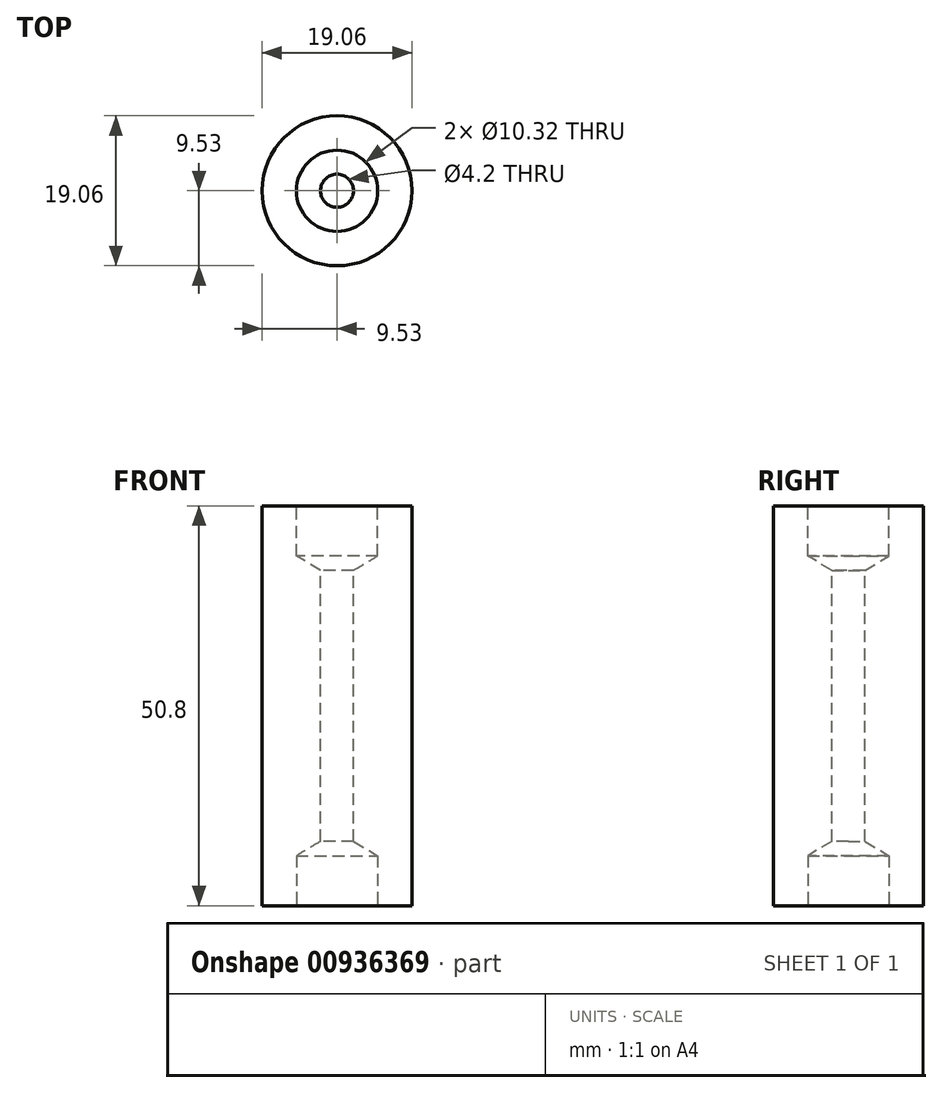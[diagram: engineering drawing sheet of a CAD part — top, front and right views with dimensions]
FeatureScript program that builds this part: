
annotation { "Feature Type Name" : "Feature", "Feature Type Description" : "" }
export const myFeature = defineFeature(function(context is Context, id is Id, definition is map)
    precondition{}
    {
        {
            var Q0;
            Q0=qCreatedBy(makeId("Top.planeOp"),FACE);
            cPlane(context, id + "F0", {"entities" : qUnion([Q0]), "cplaneType" : CPlaneType.OFFSET, "offset" : 50.8 * mm, "oppositeDirection" : true, "width" : 152.4 * mm, "height" : 152.4 * mm});
        }
        {
            var Q0;
            Q0=qCreatedBy(makeId("Top.planeOp"),FACE);
            var sketch = newSketch(context, id + "F1", { "sketchPlane" : qUnion([Q0])});
            skCircle(sketch, "E0", {"center": v(0, 0) * mm, "radius": 9.53 * mm});
            skSolve(sketch);
        }
        {
            var Q0;
            Q0=makeQuery(id+"F1.imprint","IMPRINT",FACE,{"disambiguationData":[TD([[makeQuery(id+"F1.imprint","IMPRINT",EDGE,{"derivedFrom":sQuery(id+"F1.wireOp",EDGE,"E0")}),1.0]])]});
            var Q1;
            Q1=qCreatedBy(id+"F0.planeOp",FACE);
            extrude(context, id + "F2", {"entities" : qUnion([Q0]), "endBound" : BoundingType.UP_TO_SURFACE, "oppositeDirection" : true, "depth" : 25.4 * mm, "endBoundEntityFace" : qUnion([Q1]), "offsetDistance" : 25.4 * mm});
        }
        {
            var Q0;
            Q0=qCreatedBy(makeId("Top.planeOp"),FACE);
            var sketch = newSketch(context, id + "F3", { "sketchPlane" : qUnion([Q0])});
            skPoint(sketch, "E1", {"position": v(0, 0) * mm});
            skSolve(sketch);
        }
        {
            var Q0;
            Q0=qCreatedBy(id+"F0.planeOp",FACE);
            var sketch = newSketch(context, id + "F4", { "sketchPlane" : qUnion([Q0])});
            skPoint(sketch, "E2", {"position": v(0, 0) * mm});
            skSolve(sketch);
        }
        {
            var Q0;
            Q0=sQuery(id+"F3.wireOp",VERTEX,"E1");
            var Q1;
            Q1=makeQuery(id+"F2.opExtrude","SWEPT_BODY",BODY,{"disambiguationData":[OSD([sQuery(id+"F1.wireOp",EDGE,"E0")])]});
            hole(context, id + "F5", {"style" : HoleStyle.SIMPLE, "endStyle" : HoleEndStyle.THROUGH, "standardTappedOrClearance" : lookupTablePath({ "standard" : "ISO", "engagement" : "75%", "pitch" : "0.8 mm", "size" : "M5", "type" : "Tapped" }), "standardBlindInLast" : lookupTablePath({ "standard" : "ISO", "fit" : "Normal", "engagement" : "75%", "pitch" : "0.8 mm", "size" : "M5", "type" : "Clearance & tapped" }), "holeDiameter" : 4.2 * mm, "majorDiameter" : 5 * mm, "showTappedDepth" : true, "tappedDepth" : 12.7 * mm, "tapClearance" : 3, "locations" : qUnion([Q0]), "scope" : qUnion([Q1])});
        }
        {
            var Q0;
            Q0=sQuery(id+"F4.wireOp",VERTEX,"E2");
            var Q1;
            Q1=makeQuery(id+"F2.opExtrude","SWEPT_BODY",BODY,{"disambiguationData":[OSD([sQuery(id+"F1.wireOp",EDGE,"E0")])]});
            hole(context, id + "F6", {"style" : HoleStyle.SIMPLE, "endStyle" : HoleEndStyle.BLIND, "oppositeDirection" : true, "holeDiameter" : 10.32 * mm, "majorDiameter" : 6.35 * mm, "holeDepth" : 6.35 * mm, "tappedDepth" : 12.7 * mm, "tapClearance" : 3, "startFromSketch" : true, "locations" : qUnion([Q0]), "scope" : qUnion([Q1])});
        }
        {
            var Q0;
            Q0=qCreatedBy(makeId("Top.planeOp"),FACE);
            var sketch = newSketch(context, id + "F7", { "sketchPlane" : qUnion([Q0])});
            skPoint(sketch, "E3", {"position": v(0, 0) * mm});
            skSolve(sketch);
        }
        {
            var Q0;
            Q0=sQuery(id+"F7.wireOp",VERTEX,"E3");
            var Q1;
            Q1=makeQuery(id+"F2.opExtrude","SWEPT_BODY",BODY,{"disambiguationData":[OSD([sQuery(id+"F1.wireOp",EDGE,"E0")])]});
            hole(context, id + "F8", {"style" : HoleStyle.SIMPLE, "endStyle" : HoleEndStyle.BLIND, "holeDiameter" : 10.32 * mm, "majorDiameter" : 6.35 * mm, "holeDepth" : 6.35 * mm, "tappedDepth" : 12.7 * mm, "tapClearance" : 3, "locations" : qUnion([Q0]), "scope" : qUnion([Q1])});
        }
    });
